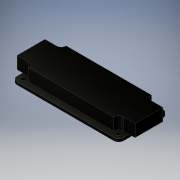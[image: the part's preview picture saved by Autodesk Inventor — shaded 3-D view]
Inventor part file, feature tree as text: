
AUTODESK INVENTOR PART (.ipt)
format: ipt  version: 2019 (Build 230136000, 136)  size: 161,792 bytes
history: native  units: mm
features: extrude x2, sketch x2
ambient origin geometry x8: Origin, YZ Plane, XZ Plane, XY Plane, X Axis, Y Axis, Z Axis, Center Point
bodies: Solid1 (feature_tree)
feature tree (4):
  extrude  "Extrusion1"  Depth=30.0mm
  extrude  "Extrusion3"  Depth=7.5mm
  sketch  "Sketch1"  dims[d0=65.0mm d1=30.0mm]
  sketch  "Sketch2"  dims[d2=3.0mm d3=2.5mm d4=3.5mm d5=3.5mm d6=20.0mm d8=23.0mm d9=20.0mm d11=58.0mm d14=1.6mm d15=0.0mm d17=6.0mm d18=20.0mm d20=23.0mm d21=20.0mm d23=58.0mm d28=7.0mm d29=7.0mm d30=7.5mm d31=0.0mm]
